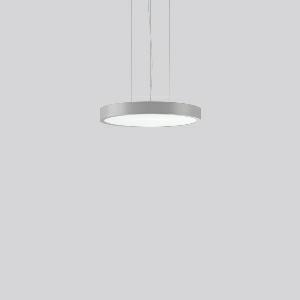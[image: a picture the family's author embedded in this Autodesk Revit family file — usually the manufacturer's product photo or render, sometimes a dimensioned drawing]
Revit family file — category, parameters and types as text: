
# Revit family: triona_round_p_312422_004_2_76_ccb2
name_source: partatom
category: Lighting Fixtures
units: mm (PartAtom-declared; Revit-internal decimal feet)

## family parameters
Cut with Voids When Loaded = No
Host = Face
Light Source = No
Part Type = Normal
Room Calculation Point = No
Round Connector Dimension = Use Diameter
Shared = No

## types (1)
- TuneableWhite 846 (1 x LED Modul 846, 3050 lm, 4600)
    Apparent Load = 38 VA
    CIE Flux Codes = 48 79 96 82 100
    Color Rendering = 80
    Color Temperature = 4600
    Default Elevation = 1800 mm
    Description = Series: TRIONA round
Decorative round LED pendant-mounted surface luminaire. Flat, seamless frame: aluminium extrusion profile, powder coated. Cover made of sheet steel, powder-coated. Canopy made of aluminium, powder-coated. Direct light emission through a diffuser plastic opal. Indirect light emission through a flush diffuser made of satin-finish plastic. Lightguide and diffuser made of non-yellowing plastic (PMMA). Lateral light emission (RZB SIDELITE technology) for above-average homogeneous light distribution. Direct 70%, indirect 30% light emission. Tunable white versions, dynamically adjustable from 2700 K to 6500 K. 3-point steel cable suspension, steplessly adjustable. Easy installation with transparent, adjustable pendant cable and canopy with magnetic fixing. Driver integrated. 
Colour: silver, matt (approx. RAL 9006)
Diameter: 461 mm
Height: 52 mm
Suspension length: 500-1200 mm
Lamp: LED
Socket: without socket
Colour temperature: 2700K - 6500K
Colour rendering index (CRI): 80
System power: 38 W
Rated luminous flux: 3050 lm
Luminous efficiency: 80 lm/W
System power 2: 39 W
Rated luminous flux 2: 2900 lm
Luminous efficiency 2: 74 lm/W
System power 3: 39 W
Rated luminous flux 3: 2950 lm
Luminous efficiency 3: 76 lm/W
Control gear: Converter, dimmable, DALI
Protection class: I
Type of protection: IP 20
    Height = 52 mm  [stored 0.170604 ft]
    Lamp = 1 x LED Modul 846
    Lamp Light Flux = 3050 lm
    Lamp count = 1
    Length = 461 mm
    Lifetime = 50000 h
    Luminous efficacy = 80 lm/W
    Manufacturer = RZB
    ModVariant = No
    Model = 312422.004.2.76
    Mounting Place = Ceiling
    Mounting Type = Pendant
    Number of Poles = 1
    OnlyDefault = Yes
    Power Factor = 1
    Product Name = TRIONA round P
    Product group = Pendant modular luminaires
    ProductGroupID = 906
    Protection Class = Protection class I
    Protection Degree = IP 20
    RLX_Detail_Level = 1
    RLX_Emergency_Light_Flux = 0 lm
    RLX_Emergency_Type = 0
    RLX_Emergency_Type_DB = No
    RlxData = <blob elided: 34297 chars, md5=e8c0382f>
    Socket = socket
    Standby Power = 0 W
    System Light Flux = 3050 lm
    System Power = 38 W
    Type Comments = TuneableWhite 846
    Type Image = 312422.004.jpg
    URL = http://relux.com
    VarID = tuneablewhite_846
    Voltage = 230 V
    Voltage Range = 220-240 V
    Weight = 0.00 kg
    Width = 0 mm  [stored 0 ft]

note: [stored X ft] marks values corroborated as IEEE doubles in the binary element streams (Revit-internal decimal feet)

## geometry (parser evidence)
native form markers: Blend x4, Sweep x12
no freeform markers — native parametric forms only
